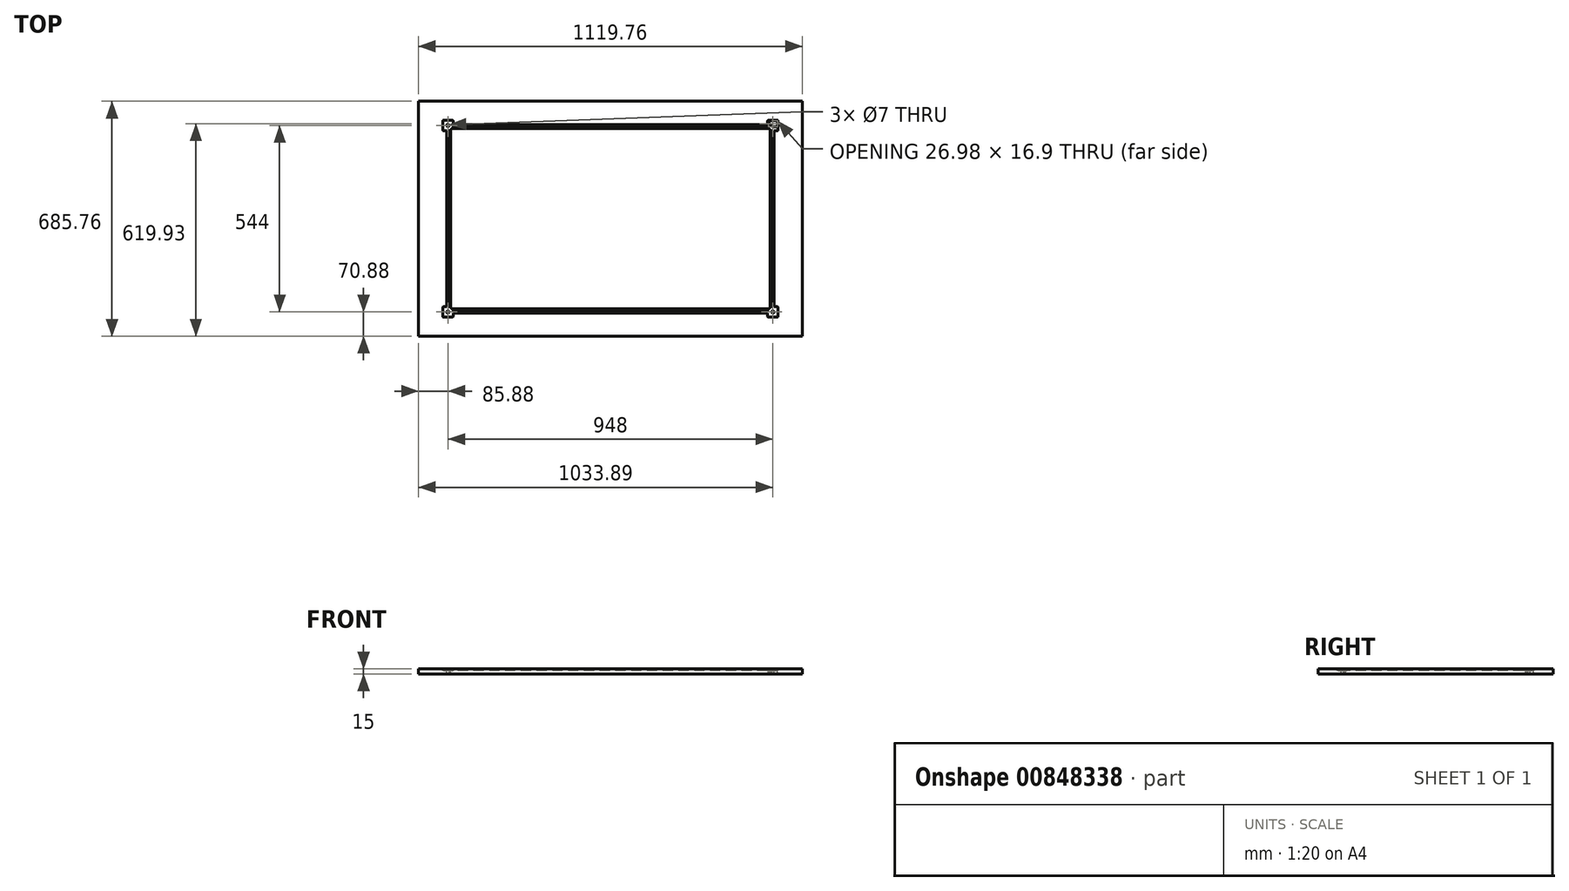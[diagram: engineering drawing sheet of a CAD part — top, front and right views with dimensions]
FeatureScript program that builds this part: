
annotation { "Feature Type Name" : "Feature", "Feature Type Description" : "" }
export const myFeature = defineFeature(function(context is Context, id is Id, definition is map)
    precondition{}
    {
        {
            var Q0;
            Q0=qCreatedBy(makeId("Top.planeOp"),FACE);
            var sketch = newSketch(context, id + "F0", { "sketchPlane" : qUnion([Q0])});
            skLineSegment(sketch, "E0.bottom", {"start": v(-559.88, 342.87) * mm, "end": v(559.88, 342.87) * mm});
            skLineSegment(sketch, "E0.top", {"start": v(-559.88, -342.88) * mm, "end": v(559.88, -342.88) * mm});
            skLineSegment(sketch, "E0.left", {"start": v(-559.88, 342.87) * mm, "end": v(-559.88, -342.88) * mm});
            skLineSegment(sketch, "E0.right", {"start": v(559.88, 342.87) * mm, "end": v(559.88, -342.88) * mm});
            skSolve(sketch);
        }
        {
            var Q0;
            Q0=qSketchRegion(id+"F0",true);
            extrude(context, id + "F1", {"entities" : qUnion([Q0]), "depth" : 15 * mm, "offsetDistance" : 25 * mm});
        }
        {
            var Q0;
            Q0=makeQuery(id+"F1.opExtrude","CAP_FACE",FACE,{"disambiguationData":[OSD([sQuery(id+"F0.wireOp",EDGE,"E0.bottom"),sQuery(id+"F0.wireOp",EDGE,"E0.top"),sQuery(id+"F0.wireOp",EDGE,"E0.left"),sQuery(id+"F0.wireOp",EDGE,"E0.right")])],"isStart":false});
            var sketch = newSketch(context, id + "F2", { "sketchPlane" : qUnion([Q0])});
            skLineSegment(sketch, "E1", {"start": v(0, 275) * mm, "end": v(-458.5, 275) * mm});
            skLineSegment(sketch, "E2", {"start": v(-458.5, 275) * mm, "end": v(-458.5, 284.5) * mm});
            skArc(sketch, "E3", {"start": v(-458.5, 284.5) * mm, "mid": v(-459.38, 286.62) * mm, "end": v(-461.5, 287.5) * mm});
            skLineSegment(sketch, "E4", {"start": v(-461.5, 287.5) * mm, "end": v(-486.5, 287.5) * mm});
            skArc(sketch, "E5", {"start": v(-486.5, 287.5) * mm, "mid": v(-488.62, 286.62) * mm, "end": v(-489.5, 284.5) * mm});
            skLineSegment(sketch, "E6", {"start": v(-489.5, 284.5) * mm, "end": v(-489.5, 259.5) * mm});
            skArc(sketch, "E7", {"start": v(-489.5, 259.5) * mm, "mid": v(-488.62, 257.38) * mm, "end": v(-486.5, 256.5) * mm});
            skLineSegment(sketch, "E8", {"start": v(-486.5, 256.5) * mm, "end": v(-477, 256.5) * mm});
            skLineSegment(sketch, "E9", {"start": v(-477, 256.5) * mm, "end": v(-477, 0) * mm});
            skLineSegment(sketch, "E10", {"start": v(-477, 0) * mm, "end": v(-471, 0) * mm});
            skLineSegment(sketch, "E11", {"start": v(-471, 0) * mm, "end": v(-471, 256.5) * mm});
            skLineSegment(sketch, "E12", {"start": v(-471, 256.5) * mm, "end": v(-461.5, 256.5) * mm});
            skArc(sketch, "E13", {"start": v(-461.5, 256.5) * mm, "mid": v(-459.38, 257.38) * mm, "end": v(-458.5, 259.5) * mm});
            skLineSegment(sketch, "E14", {"start": v(-458.5, 259.5) * mm, "end": v(-458.5, 269) * mm});
            skLineSegment(sketch, "E15", {"start": v(-458.5, 269) * mm, "end": v(0, 269) * mm});
            skLineSegment(sketch, "E16", {"start": v(0, 269) * mm, "end": v(0, 275) * mm});
            skLineSegment(sketch, "E17", {"start": v(0, 342.87) * mm, "end": v(0, -342.88) * mm, "construction": true});
            skLineSegment(sketch, "E18", {"start": v(-559.88, 0) * mm, "end": v(559.88, 0) * mm, "construction": true});
            skLineSegment(sketch, "E19.MirrorCS", {"start": v(458.5, 269) * mm, "end": v(0, 269) * mm});
            skLineSegment(sketch, "E20.MirrorCS", {"start": v(0, 275) * mm, "end": v(458.5, 275) * mm});
            skLineSegment(sketch, "E21.MirrorCS", {"start": v(458.5, 275) * mm, "end": v(458.5, 284.5) * mm});
            skArc(sketch, "E22.MirrorCS", {"start": v(458.5, 284.5) * mm, "mid": v(459.38, 286.62) * mm, "end": v(461.5, 287.5) * mm});
            skLineSegment(sketch, "E23.MirrorCS", {"start": v(461.5, 287.5) * mm, "end": v(486.5, 287.5) * mm});
            skArc(sketch, "E24.MirrorCS", {"start": v(486.5, 287.5) * mm, "mid": v(488.62, 286.62) * mm, "end": v(489.5, 284.5) * mm});
            skLineSegment(sketch, "E25.MirrorCS", {"start": v(489.5, 284.5) * mm, "end": v(489.5, 259.5) * mm});
            skArc(sketch, "E26.MirrorCS", {"start": v(489.5, 259.5) * mm, "mid": v(488.62, 257.38) * mm, "end": v(486.5, 256.5) * mm});
            skLineSegment(sketch, "E27.MirrorCS", {"start": v(486.5, 256.5) * mm, "end": v(477, 256.5) * mm});
            skLineSegment(sketch, "E28.MirrorCS", {"start": v(477, 256.5) * mm, "end": v(477, 0) * mm});
            skLineSegment(sketch, "E29.MirrorCS", {"start": v(471, 0) * mm, "end": v(471, 256.5) * mm});
            skLineSegment(sketch, "E30.MirrorCS", {"start": v(471, 256.5) * mm, "end": v(461.5, 256.5) * mm});
            skArc(sketch, "E31.MirrorCS", {"start": v(461.5, 256.5) * mm, "mid": v(459.38, 257.38) * mm, "end": v(458.5, 259.5) * mm});
            skLineSegment(sketch, "E32.MirrorCS", {"start": v(458.5, 259.5) * mm, "end": v(458.5, 269) * mm});
            skLineSegment(sketch, "E33.MirrorCS", {"start": v(477, -256.5) * mm, "end": v(477, 0) * mm});
            skLineSegment(sketch, "E34.MirrorCS", {"start": v(471, 0) * mm, "end": v(471, -256.5) * mm});
            skLineSegment(sketch, "E35.MirrorCS", {"start": v(486.5, -256.5) * mm, "end": v(477, -256.5) * mm});
            skArc(sketch, "E36.MirrorCS", {"start": v(489.5, -259.5) * mm, "mid": v(488.62, -257.38) * mm, "end": v(486.5, -256.5) * mm});
            skLineSegment(sketch, "E37.MirrorCS", {"start": v(489.5, -284.5) * mm, "end": v(489.5, -259.5) * mm});
            skArc(sketch, "E38.MirrorCS", {"start": v(486.5, -287.5) * mm, "mid": v(488.62, -286.62) * mm, "end": v(489.5, -284.5) * mm});
            skLineSegment(sketch, "E39.MirrorCS", {"start": v(461.5, -287.5) * mm, "end": v(486.5, -287.5) * mm});
            skArc(sketch, "E40.MirrorCS", {"start": v(458.5, -284.5) * mm, "mid": v(459.38, -286.62) * mm, "end": v(461.5, -287.5) * mm});
            skLineSegment(sketch, "E41.MirrorCS", {"start": v(458.5, -275) * mm, "end": v(458.5, -284.5) * mm});
            skLineSegment(sketch, "E42.MirrorCS", {"start": v(0, -275) * mm, "end": v(458.5, -275) * mm});
            skLineSegment(sketch, "E43.MirrorCS", {"start": v(458.5, -269) * mm, "end": v(0, -269) * mm});
            skLineSegment(sketch, "E44.MirrorCS", {"start": v(458.5, -259.5) * mm, "end": v(458.5, -269) * mm});
            skArc(sketch, "E45.MirrorCS", {"start": v(461.5, -256.5) * mm, "mid": v(459.38, -257.38) * mm, "end": v(458.5, -259.5) * mm});
            skLineSegment(sketch, "E46.MirrorCS", {"start": v(471, -256.5) * mm, "end": v(461.5, -256.5) * mm});
            skLineSegment(sketch, "E47.MirrorCS", {"start": v(-458.5, -269) * mm, "end": v(0, -269) * mm});
            skLineSegment(sketch, "E48.MirrorCS", {"start": v(0, -275) * mm, "end": v(-458.5, -275) * mm});
            skLineSegment(sketch, "E49.MirrorCS", {"start": v(-477, -256.5) * mm, "end": v(-477, 0) * mm});
            skLineSegment(sketch, "E50.MirrorCS", {"start": v(-471, 0) * mm, "end": v(-471, -256.5) * mm});
            skLineSegment(sketch, "E51.MirrorCS", {"start": v(-471, -256.5) * mm, "end": v(-461.5, -256.5) * mm});
            skArc(sketch, "E52.MirrorCS", {"start": v(-461.5, -256.5) * mm, "mid": v(-459.38, -257.38) * mm, "end": v(-458.5, -259.5) * mm});
            skLineSegment(sketch, "E53.MirrorCS", {"start": v(-458.5, -259.5) * mm, "end": v(-458.5, -269) * mm});
            skLineSegment(sketch, "E54.MirrorCS", {"start": v(-458.5, -275) * mm, "end": v(-458.5, -284.5) * mm});
            skArc(sketch, "E55.MirrorCS", {"start": v(-458.5, -284.5) * mm, "mid": v(-459.38, -286.62) * mm, "end": v(-461.5, -287.5) * mm});
            skLineSegment(sketch, "E56.MirrorCS", {"start": v(-461.5, -287.5) * mm, "end": v(-486.5, -287.5) * mm});
            skArc(sketch, "E57.MirrorCS", {"start": v(-486.5, -287.5) * mm, "mid": v(-488.62, -286.62) * mm, "end": v(-489.5, -284.5) * mm});
            skLineSegment(sketch, "E58.MirrorCS", {"start": v(-489.5, -284.5) * mm, "end": v(-489.5, -259.5) * mm});
            skArc(sketch, "E59.MirrorCS", {"start": v(-489.5, -259.5) * mm, "mid": v(-488.62, -257.38) * mm, "end": v(-486.5, -256.5) * mm});
            skLineSegment(sketch, "E60.MirrorCS", {"start": v(-486.5, -256.5) * mm, "end": v(-477, -256.5) * mm});
            skSolve(sketch);
        }
        {
            var Q0;
            Q0=qSketchRegion(id+"F2",true);
            extrude(context, id + "F3", {"entities" : qUnion([Q0]), "operationType" : NewBodyOperationType.REMOVE, "oppositeDirection" : true, "depth" : 5 * mm, "offsetDistance" : 25 * mm});
        }
        {
            var Q0;
            Q0=makeQuery(id+"F3.boolean.opBoolean","COPY",FACE,{"derivedFrom":makeQuery(id+"F3.opExtrude","CAP_FACE",FACE,{"disambiguationData":[OSD([sQuery(id+"F2.wireOp",EDGE,"E1"),sQuery(id+"F2.wireOp",EDGE,"E2"),sQuery(id+"F2.wireOp",EDGE,"E3"),sQuery(id+"F2.wireOp",EDGE,"E4"),sQuery(id+"F2.wireOp",EDGE,"E5"),sQuery(id+"F2.wireOp",EDGE,"E6"),sQuery(id+"F2.wireOp",EDGE,"E7"),sQuery(id+"F2.wireOp",EDGE,"E8"),sQuery(id+"F2.wireOp",EDGE,"E9"),sQuery(id+"F2.wireOp",EDGE,"E11"),sQuery(id+"F2.wireOp",EDGE,"E12"),sQuery(id+"F2.wireOp",EDGE,"E13"),sQuery(id+"F2.wireOp",EDGE,"E14"),sQuery(id+"F2.wireOp",EDGE,"E15"),sQuery(id+"F2.wireOp",EDGE,"E19.MirrorCS"),sQuery(id+"F2.wireOp",EDGE,"E20.MirrorCS"),sQuery(id+"F2.wireOp",EDGE,"E21.MirrorCS"),sQuery(id+"F2.wireOp",EDGE,"E22.MirrorCS"),sQuery(id+"F2.wireOp",EDGE,"E23.MirrorCS"),sQuery(id+"F2.wireOp",EDGE,"E24.MirrorCS"),sQuery(id+"F2.wireOp",EDGE,"E25.MirrorCS"),sQuery(id+"F2.wireOp",EDGE,"E26.MirrorCS"),sQuery(id+"F2.wireOp",EDGE,"E27.MirrorCS"),sQuery(id+"F2.wireOp",EDGE,"E28.MirrorCS"),sQuery(id+"F2.wireOp",EDGE,"E29.MirrorCS"),sQuery(id+"F2.wireOp",EDGE,"E30.MirrorCS"),sQuery(id+"F2.wireOp",EDGE,"E31.MirrorCS"),sQuery(id+"F2.wireOp",EDGE,"E32.MirrorCS"),sQuery(id+"F2.wireOp",EDGE,"E33.MirrorCS"),sQuery(id+"F2.wireOp",EDGE,"E34.MirrorCS"),sQuery(id+"F2.wireOp",EDGE,"E35.MirrorCS"),sQuery(id+"F2.wireOp",EDGE,"E36.MirrorCS"),sQuery(id+"F2.wireOp",EDGE,"E37.MirrorCS"),sQuery(id+"F2.wireOp",EDGE,"E38.MirrorCS"),sQuery(id+"F2.wireOp",EDGE,"E39.MirrorCS"),sQuery(id+"F2.wireOp",EDGE,"E40.MirrorCS"),sQuery(id+"F2.wireOp",EDGE,"E41.MirrorCS"),sQuery(id+"F2.wireOp",EDGE,"E42.MirrorCS"),sQuery(id+"F2.wireOp",EDGE,"E43.MirrorCS"),sQuery(id+"F2.wireOp",EDGE,"E44.MirrorCS"),sQuery(id+"F2.wireOp",EDGE,"E45.MirrorCS"),sQuery(id+"F2.wireOp",EDGE,"E46.MirrorCS"),sQuery(id+"F2.wireOp",EDGE,"E47.MirrorCS"),sQuery(id+"F2.wireOp",EDGE,"E48.MirrorCS"),sQuery(id+"F2.wireOp",EDGE,"E49.MirrorCS"),sQuery(id+"F2.wireOp",EDGE,"E50.MirrorCS"),sQuery(id+"F2.wireOp",EDGE,"E51.MirrorCS"),sQuery(id+"F2.wireOp",EDGE,"E52.MirrorCS"),sQuery(id+"F2.wireOp",EDGE,"E53.MirrorCS"),sQuery(id+"F2.wireOp",EDGE,"E54.MirrorCS"),sQuery(id+"F2.wireOp",EDGE,"E55.MirrorCS"),sQuery(id+"F2.wireOp",EDGE,"E56.MirrorCS"),sQuery(id+"F2.wireOp",EDGE,"E57.MirrorCS"),sQuery(id+"F2.wireOp",EDGE,"E58.MirrorCS"),sQuery(id+"F2.wireOp",EDGE,"E59.MirrorCS"),sQuery(id+"F2.wireOp",EDGE,"E60.MirrorCS")])],"isStart":false})});
            var sketch = newSketch(context, id + "F4", { "sketchPlane" : qUnion([Q0])});
            skCircle(sketch, "E61", {"center": v(-474, 272) * mm, "radius": 3.5 * mm});
            skPoint(sketch, "E61.centerSnap0", {"position": v(-474, 287.5) * mm});
            skCircle(sketch, "E62", {"center": v(474, -272) * mm, "radius": 3.5 * mm});
            skCircle(sketch, "E63", {"center": v(-474, -272) * mm, "radius": 3.5 * mm});
            skLineSegment(sketch, "E64", {"start": v(463.5, 285.5) * mm, "end": v(484.5, 285.5) * mm});
            skArc(sketch, "E65", {"start": v(474, 268.6) * mm, "mid": v(472.66, 268.88) * mm, "end": v(471.53, 269.66) * mm});
            skLineSegment(sketch, "E66", {"start": v(471.53, 269.66) * mm, "end": v(461.32, 280.44) * mm});
            skArc(sketch, "E67", {"start": v(463.5, 285.5) * mm, "mid": v(460.74, 283.69) * mm, "end": v(461.32, 280.44) * mm});
            skArc(sketch, "E68", {"start": v(487.5, 282.5) * mm, "mid": v(486.62, 284.62) * mm, "end": v(484.5, 285.5) * mm});
            skLineSegment(sketch, "E69", {"start": v(474, 268.6) * mm, "end": v(484.5, 268.6) * mm});
            skArc(sketch, "E70", {"start": v(484.5, 268.6) * mm, "mid": v(486.62, 269.48) * mm, "end": v(487.5, 271.6) * mm});
            skLineSegment(sketch, "E71", {"start": v(487.5, 271.6) * mm, "end": v(487.5, 282.5) * mm});
            skSolve(sketch);
        }
        {
            var Q0;
            Q0=qSketchRegion(id+"F4",true);
            extrude(context, id + "F5", {"entities" : qUnion([Q0]), "operationType" : NewBodyOperationType.REMOVE, "endBound" : BoundingType.UP_TO_NEXT, "oppositeDirection" : true, "depth" : 25 * mm, "offsetDistance" : 25 * mm});
        }
        {
            var Q0;
            Q0=makeQuery(id+"F3.boolean.opBoolean","SPLIT",FACE,{"disambiguationData":[TD([makeQuery(id+"F3.opExtrude","SWEPT_FACE",FACE,{"disambiguationData":[OSD([sQuery(id+"F2.wireOp",EDGE,"E12")])]})])],"derivedFrom":makeQuery(id+"F1.opExtrude","CAP_FACE",FACE,{"disambiguationData":[OSD([sQuery(id+"F0.wireOp",EDGE,"E0.bottom"),sQuery(id+"F0.wireOp",EDGE,"E0.top"),sQuery(id+"F0.wireOp",EDGE,"E0.left"),sQuery(id+"F0.wireOp",EDGE,"E0.right")])],"isStart":false})});
            var sketch = newSketch(context, id + "F6", { "sketchPlane" : qUnion([Q0])});
            skLineSegment(sketch, "E72", {"start": v(-462.5, 262.5) * mm, "end": v(462.5, 262.5) * mm});
            skArc(sketch, "E73", {"start": v(462.5, 262.5) * mm, "mid": v(464.62, 261.62) * mm, "end": v(465.5, 259.5) * mm});
            skLineSegment(sketch, "E74", {"start": v(465.5, 259.5) * mm, "end": v(465.5, -259.5) * mm});
            skArc(sketch, "E75", {"start": v(-462.5, 262.5) * mm, "mid": v(-464.62, 261.62) * mm, "end": v(-465.5, 259.5) * mm});
            skLineSegment(sketch, "E76", {"start": v(-465.5, 259.5) * mm, "end": v(-465.5, -259.5) * mm});
            skArc(sketch, "E77", {"start": v(-465.5, -259.5) * mm, "mid": v(-464.62, -261.62) * mm, "end": v(-462.5, -262.5) * mm});
            skLineSegment(sketch, "E78", {"start": v(-462.5, -262.5) * mm, "end": v(462.5, -262.5) * mm});
            skArc(sketch, "E79", {"start": v(462.5, -262.5) * mm, "mid": v(464.62, -261.62) * mm, "end": v(465.5, -259.5) * mm});
            skSolve(sketch);
        }
        {
            var Q0;
            Q0 = qSketchRegion(id + "F6", true);
            extrude(context, id + "F7", {"entities" : qUnion([Q0]), "operationType" : NewBodyOperationType.REMOVE, "endBound" : BoundingType.UP_TO_NEXT, "oppositeDirection" : true, "depth" : 25 * mm, "offsetDistance" : 25 * mm});
        }
        {
            var Q0;
            Q0=qCreatedBy(makeId("Top.planeOp"),FACE);
            cPlane(context, id + "F8", {"entities" : qUnion([Q0]), "cplaneType" : CPlaneType.OFFSET, "offset" : 25 * mm, "width" : 150 * mm, "height" : 150 * mm});
        }
    });
